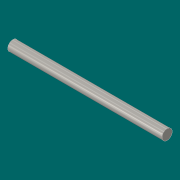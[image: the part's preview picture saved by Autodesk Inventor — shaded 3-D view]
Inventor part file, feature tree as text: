
AUTODESK INVENTOR PART (.ipt)
format: ipt  version: 2016 (Build 200138000, 138)  size: 77,312 bytes
history: native  units: mm
features: extrude x1, sketch x1
ambient origin geometry x8: Origin, YZ Plane, XZ Plane, XY Plane, X Axis, Y Axis, Z Axis, Center Point
bodies: Solid1 (feature_tree)
feature tree (2):
  extrude  "Extrusion1"  Depth=120.0mm
  sketch  "Sketch1"  dims[d0=8.0mm d1=120.0mm d2=0.0mm]
